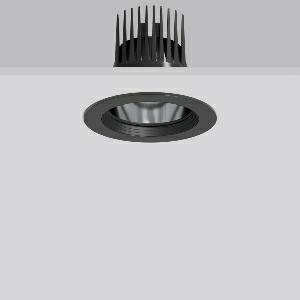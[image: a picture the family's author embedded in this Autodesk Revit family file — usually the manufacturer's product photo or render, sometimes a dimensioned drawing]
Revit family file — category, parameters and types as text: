
# Revit family: heledon_maxi_e_901777_003_76_e917
name_source: partatom
category: Lighting Fixtures
units: mm (PartAtom-declared; Revit-internal decimal feet)

## family parameters
Cut with Voids When Loaded = No
Host = Face
Light Source = No
Part Type = Normal
Room Calculation Point = No
Round Connector Dimension = Use Diameter
Shared = No

## types (1)
- HELEDON maxi E (1 x LED Modul 920 meat+, 2200 lm, 2000)
    Apparent Load = 33 VA
    Approval mark = CE
    CIE Flux Codes = 100 100 100 100 100
    Color Rendering = 90
    Color Temperature = 2000
    Default Elevation = 1800 mm
    Description = Series: HELEDON maxi
Round recessed downlight. Housing: die-cast aluminium, powder-coated. Black plastic ring and recessed LED to prevent glare from the side. Optical assembly with reflector made of MIRO-Silver with 98% total light reflection for outstanding efficiency - can be changed without tools. Special LED for illumination of meat included. Suitable for Recessed ceiling mounting. Installation without tools thanks to spring fastening system. Including separate LED converter with connecting cable 600 mm.High quality converter without flickering and stroboscopic effect. Through-wiring box (5 pole) available as accessory. The following accessories can be mounted without use of tools: interchangeable lenses, decorative glasses, honeycomb louvre, clear and frosted diffusers, white interchangeable plastic ring. 
Colour: deep black, matt (RAL 9005)
Diameter: 162 mm
Height: 3 mm
Cut-out diameter: 152 mm
Recess height: 200 mm
Luminaire: recess height: 135 mm
Lamp: LED
Socket: without socket
Colour temperature: meat +
System power: 33 W
Rated luminous flux: 2200 lm
Luminous efficiency: 67 lm/W
Control gear: Converter, dimmable, DALI
Protection class: II
Type of protection: IP 20
    Height = 0 mm  [stored 0 ft]
    Lamp = 1 x LED Modul 920 meat+
    Lamp Light Flux = 2200 lm
    Lamp count = 1
    Length = 162 mm
    Lifetime = 50000 h
    Luminous efficacy = 67 lm/W
    Manufacturer = RZB
    ModVariant = No
    Model = 901777.003.76
    Mounting Place = Ceiling
    Mounting Type = Recessed
    Number of Poles = 1
    OnlyDefault = Yes
    Power Factor = 1
    Product Name = HELEDON maxi E
    Product group = Recessed downlights
    ProductGroupID = 402
    Protection Class = Protection class II
    Protection Degree = IP 20
    RLX_Detail_Level = 1
    RLX_Emergency_Light_Flux = 0 lm
    RLX_Emergency_Type = 0
    RLX_Emergency_Type_DB = No
    RlxData = <blob elided: 122469 chars, md5=a00b9a51>
    Socket = socket
    Standby Power = 0 W
    System Light Flux = 2200 lm
    System Power = 33 W
    Type Comments = Product without accessories
    Type Image = 901662.003.jpg
    URL = http://relux.com
    VarID = ---
    Voltage = 230 V
    Voltage Range = 220-240 V
    Weight = 0.00 kg
    Width = 0 mm  [stored 0 ft]

note: [stored X ft] marks values corroborated as IEEE doubles in the binary element streams (Revit-internal decimal feet)

## geometry (parser evidence)
native form markers: Blend x4, Sweep x11
no freeform markers — native parametric forms only
